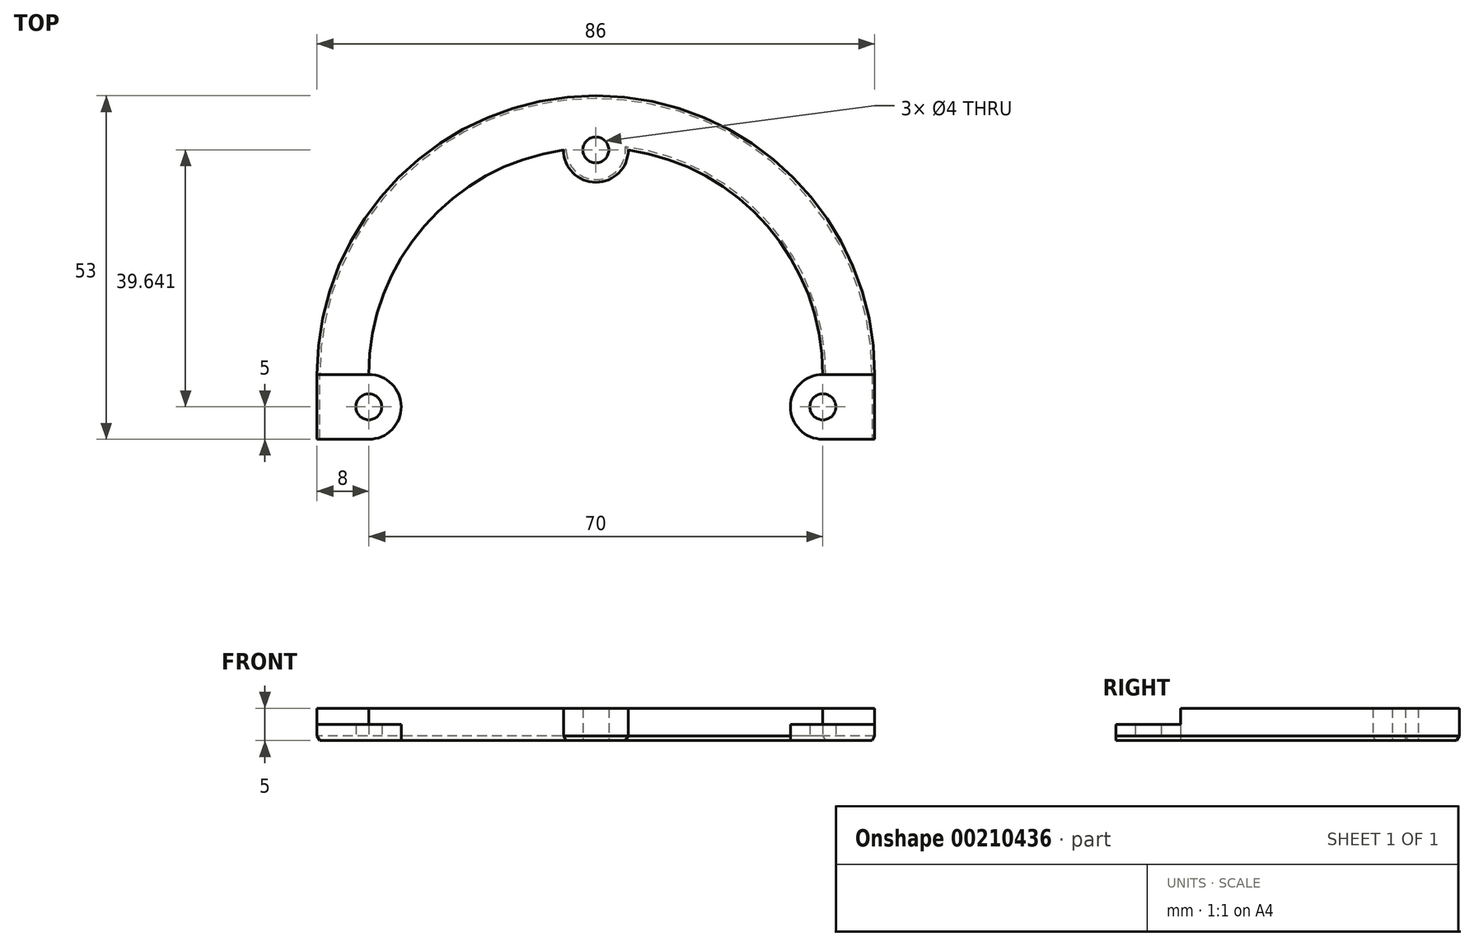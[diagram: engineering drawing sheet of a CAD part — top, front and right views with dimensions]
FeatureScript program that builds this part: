
annotation { "Feature Type Name" : "Feature", "Feature Type Description" : "" }
export const myFeature = defineFeature(function(context is Context, id is Id, definition is map)
    precondition{}
    {
        {
            var Q0;
            Q0=qCreatedBy(makeId("Top.planeOp"),FACE);
            var sketch = newSketch(context, id + "F0", { "sketchPlane" : qUnion([Q0])});
            skArc(sketch, "E0", {"start": v(35, 0) * mm, "mid": v(26.46, 22.91) * mm, "end": v(5, 34.64) * mm});
            skArc(sketch, "E1", {"start": v(43, 0) * mm, "mid": v(0, 43) * mm, "end": v(-43, 0) * mm});
            skLineSegment(sketch, "E2", {"start": v(-43, 0) * mm, "end": v(-43, -10) * mm});
            skLineSegment(sketch, "E3", {"start": v(-35, 0) * mm, "end": v(-35, 0) * mm});
            skLineSegment(sketch, "E4", {"start": v(35, 0) * mm, "end": v(35, 0) * mm});
            skLineSegment(sketch, "E5", {"start": v(43, 0) * mm, "end": v(43, -10) * mm});
            skArc(sketch, "E6", {"start": v(-35, -10) * mm, "mid": v(-30, -5) * mm, "end": v(-35, 0) * mm});
            skArc(sketch, "E7", {"start": v(35, 0) * mm, "mid": v(30, -5) * mm, "end": v(35, -10) * mm});
            skLineSegment(sketch, "E8.trimOffspring", {"start": v(35, -10) * mm, "end": v(35, -25) * mm});
            skCircle(sketch, "E9", {"center": v(-35, -5) * mm, "radius": 2 * mm});
            skCircle(sketch, "E10", {"center": v(35, -5) * mm, "radius": 2 * mm});
            skArc(sketch, "E11", {"start": v(-5, 34.64) * mm, "mid": v(0, 29.64) * mm, "end": v(5, 34.64) * mm});
            skArc(sketch, "E12.trimOffspring", {"start": v(-5, 34.64) * mm, "mid": v(-26.46, 22.91) * mm, "end": v(-35, 0) * mm});
            skCircle(sketch, "E13", {"center": v(0, 34.64) * mm, "radius": 2 * mm});
            skLineSegment(sketch, "E14", {"start": v(35, -10) * mm, "end": v(43, -10) * mm});
            skLineSegment(sketch, "E15", {"start": v(-35, -10) * mm, "end": v(-43, -10) * mm});
            skSolve(sketch);
        }
        {
            var Q0;
            Q0 = qSketchRegion(id + "F0", true);
            extrude(context, id + "F1", {"entities" : qUnion([Q0]), "depth" : 5 * mm});
        }
        {
            var Q0;
            Q0=makeQuery(id+"F1.opExtrude","CAP_EDGE",EDGE,{"disambiguationData":[OSD([sQuery(id+"F0.wireOp",EDGE,"E2")])],"isStart":true});
            var Q1;
            Q1=makeQuery(id+"F1.opExtrude","CAP_EDGE",EDGE,{"disambiguationData":[OSD([sQuery(id+"F0.wireOp",EDGE,"E3")])],"isStart":true});
            var Q2;
            Q2=makeQuery(id+"F1.opExtrude","CAP_EDGE",EDGE,{"disambiguationData":[OSD([sQuery(id+"F0.wireOp",EDGE,"E0")])],"isStart":true});
            var Q3;
            Q3=makeQuery(id+"F1.opExtrude","CAP_EDGE",EDGE,{"disambiguationData":[OSD([sQuery(id+"F0.wireOp",EDGE,"E11")])],"isStart":true});
            chamfer(context, id + "F2", {"entities" : qUnion([Q0, Q1, Q2, Q3]), "chamferType" : ChamferType.OFFSET_ANGLE, "width" : .75 * mm, "oppositeDirection" : false, "angle" : 30 * degree, "tangentPropagation" : true});
        }
        {
            var Q0;
            Q0=makeQuery(id+"F1.opExtrude","CAP_FACE",FACE,{"disambiguationData":[OSD([sQuery(id+"F0.wireOp",EDGE,"E0"),sQuery(id+"F0.wireOp",EDGE,"E1"),sQuery(id+"F0.wireOp",EDGE,"E2"),sQuery(id+"F0.wireOp",EDGE,"E3"),sQuery(id+"F0.wireOp",EDGE,"E4"),sQuery(id+"F0.wireOp",EDGE,"E5"),sQuery(id+"F0.wireOp",EDGE,"E6"),sQuery(id+"F0.wireOp",EDGE,"E7"),sQuery(id+"F0.wireOp",EDGE,"E9"),sQuery(id+"F0.wireOp",EDGE,"E10"),sQuery(id+"F0.wireOp",EDGE,"E11"),sQuery(id+"F0.wireOp",EDGE,"E12.trimOffspring"),sQuery(id+"F0.wireOp",EDGE,"E13"),sQuery(id+"F0.wireOp",EDGE,"E14"),sQuery(id+"F0.wireOp",EDGE,"E15")])],"isStart":false});
            var sketch = newSketch(context, id + "F3", { "sketchPlane" : qUnion([Q0])});
            skLineSegment(sketch, "E16", {"start": v(35, 0) * mm, "end": v(43, 0) * mm});
            skLineSegment(sketch, "E17", {"start": v(43, 0) * mm, "end": v(43, -10) * mm});
            skLineSegment(sketch, "E18", {"start": v(43, -10) * mm, "end": v(35, -10) * mm});
            skArc(sketch, "E19", {"start": v(35, 0) * mm, "mid": v(30, -5) * mm, "end": v(35, -10) * mm});
            skLineSegment(sketch, "E20", {"start": v(-43, 0) * mm, "end": v(-35, 0) * mm});
            skLineSegment(sketch, "E21", {"start": v(-43, 0) * mm, "end": v(-43, -10) * mm});
            skLineSegment(sketch, "E22", {"start": v(-43, -10) * mm, "end": v(-35, -10) * mm});
            skArc(sketch, "E23", {"start": v(-35, -10) * mm, "mid": v(-30, -5) * mm, "end": v(-35, 0) * mm});
            skSolve(sketch);
        }
        {
            var Q0;
            Q0 = qSketchRegion(id + "F3", true);
            extrude(context, id + "F4", {"entities" : qUnion([Q0]), "operationType" : NewBodyOperationType.REMOVE, "oppositeDirection" : true, "depth" : 2.5 * mm});
        }
    });
